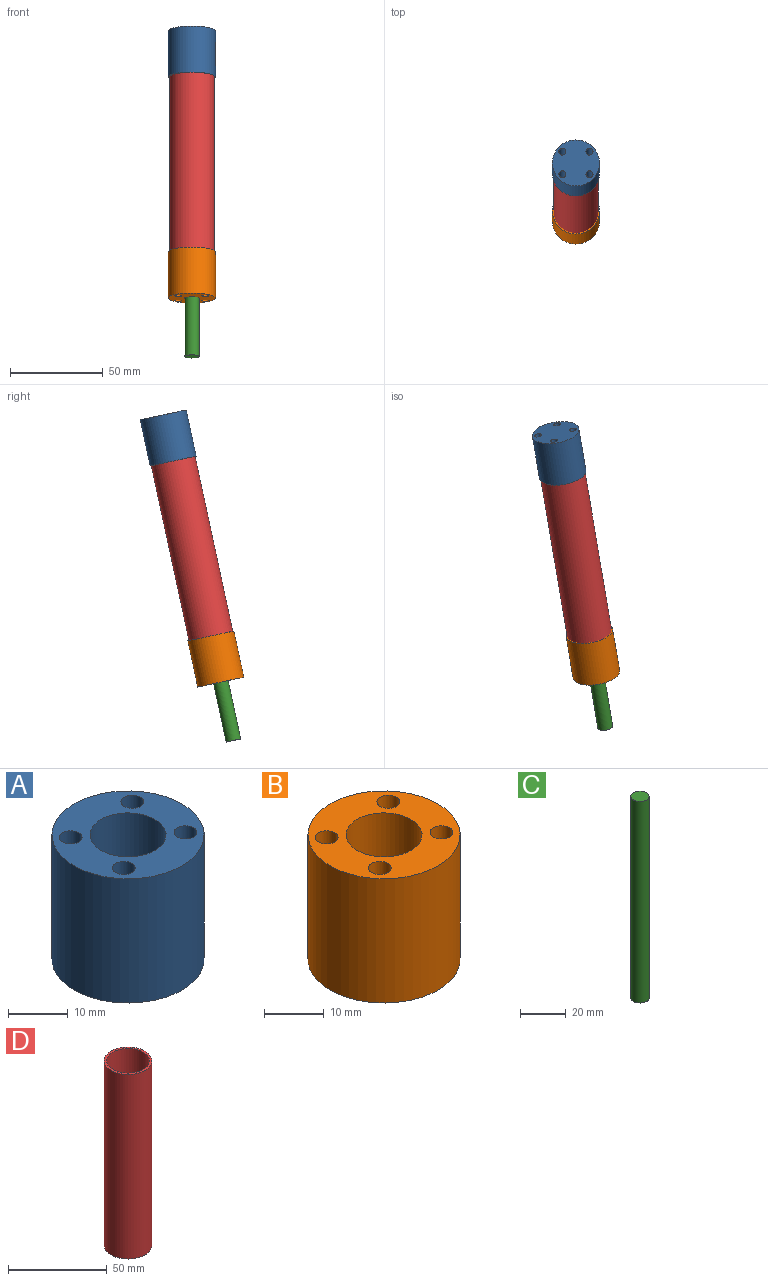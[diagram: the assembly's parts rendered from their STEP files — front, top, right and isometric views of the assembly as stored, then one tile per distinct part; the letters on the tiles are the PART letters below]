
ASSEMBLY  parts=4 mates=3
PART A: 9 faces, bbox 25.4x25.4x25.4 mm
  f0: cylinder r=6.35mm len=17.78mm, axis (0,0,-1), area 709.4mm2, adj f6,f8
  f1: cylinder r=1.91mm len=25.4mm, axis (0,0,-1), area 304mm2, adj f6,f7
  f2: cylinder r=1.91mm len=25.4mm, axis (0,0,-1), area 304mm2, adj f6,f7
  f3: cylinder r=1.91mm len=25.4mm, axis (0,0,-1), area 304mm2, adj f6,f7
  f4: cylinder r=1.91mm len=25.4mm, axis (0,0,-1), area 304mm2, adj f6,f7
  f5: cylinder r=12.7mm len=25.4mm, axis (0,0,-1), area 2026.8mm2, adj f6,f7
  f6: plane 25.4x25.4mm, normal (0,0,1), area 334.4mm2, adj f0,f1,f2,f3,f4,f5
  f7: plane 25.4x25.4mm, normal (0,0,-1), area 461.1mm2, adj f1,f2,f3,f4,f5
  f8: plane 12.7x12.7mm, normal (0,0,1), area 126.7mm2, adj f0
PART B: 10 faces, bbox 25.4x25.4x25.4 mm
  f0: cylinder r=6.35mm len=17.78mm, axis (0,0,-1), area 709.4mm2, adj f6,f9
  f1: cylinder r=1.91mm len=25.4mm, axis (0,0,-1), area 304mm2, adj f6,f7
  f2: cylinder r=1.91mm len=25.4mm, axis (0,0,-1), area 304mm2, adj f6,f7
  f3: cylinder r=1.91mm len=25.4mm, axis (0,0,-1), area 304mm2, adj f6,f7
  f4: cylinder r=1.91mm len=25.4mm, axis (0,0,-1), area 304mm2, adj f6,f7
  f5: cylinder r=12.7mm len=25.4mm, axis (0,0,-1), area 2026.8mm2, adj f6,f7
  f6: plane 25.4x25.4mm, normal (0,0,1), area 334.4mm2, adj f0,f1,f2,f3,f4,f5
  f7: plane 25.4x25.4mm, normal (0,0,-1), area 410.8mm2, adj f1,f2,f3,f4,f5,f8
  f8: cylinder r=4mm len=8mm, axis (0,0,-1), area 191.5mm2, adj f7,f9
  f9: plane 12.7x12.7mm, normal (0,0,1), area 76.4mm2, adj f0,f8
PART C: 3 faces, bbox 8x8x108 mm
  f0: cylinder r=3.99mm len=107.95mm, axis (0,0,-1), area 2704.8mm2, adj f1,f2
  f1: plane 7.98x7.98mm, normal (0,0,1), area 50mm2, adj f0
  f2: plane 7.98x7.98mm, normal (0,0,-1), area 50mm2, adj f0
PART D: 4 faces, bbox 24.1x24.1x114.3 mm
  f0: cylinder r=10.79mm len=114.3mm, axis (0,0,-1), area 7752.6mm2, adj f2,f3
  f1: cylinder r=12.06mm len=114.3mm, axis (0,0,-1), area 8664.7mm2, adj f2,f3
  f2: plane 24.13x24.13mm, normal (0,0,1), area 91.2mm2, adj f0,f1
  f3: plane 24.13x24.13mm, normal (0,0,-1), area 91.2mm2, adj f0,f1
PLACE A rot(axis=(1,0,0),167.8deg) t=(42.54,-109.72,34.73)mm
PLACE B rot(axis=(-1,0,0),12.2deg) t=(42.54,-140.77,-109.28)mm
PLACE C rot(axis=(-1,0,0),12.2deg) t=(42.54,-147.55,-140.77)mm
PLACE D rot(axis=(-1,0,0),12.2deg) t=(42.54,-139.16,-101.83)mm
MATE fastened B.f0 <-> D.f0  axis (0,0.21,0.98) through (42.54,-139.16,-101.83)mm
MATE slider B.f0 <-> C.f0  axis (0,-0.21,-0.98) through (42.54,-140.77,-109.28)mm
MATE fastened D.f0 <-> A.f0  axis (0,0.21,0.98) through (42.54,-115.07,9.9)mm
